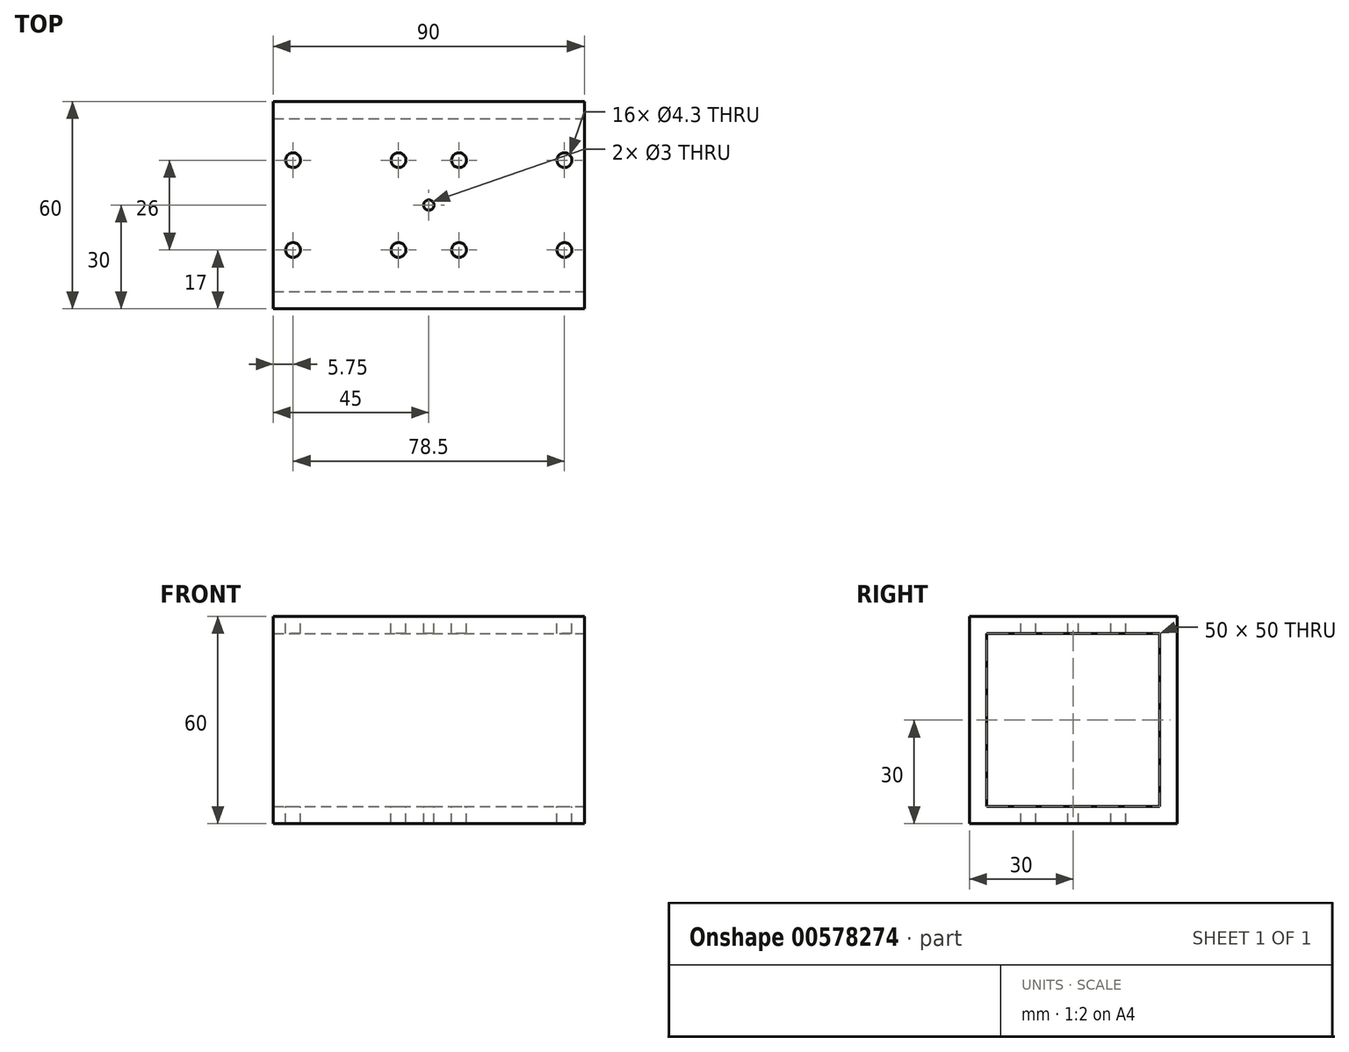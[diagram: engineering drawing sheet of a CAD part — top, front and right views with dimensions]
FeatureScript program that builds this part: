
annotation { "Feature Type Name" : "Feature", "Feature Type Description" : "" }
export const myFeature = defineFeature(function(context is Context, id is Id, definition is map)
    precondition{}
    {
        {
            var Q0;
            Q0=qCreatedBy(makeId("Top.planeOp"),FACE);
            var sketch = newSketch(context, id + "F0", { "sketchPlane" : qUnion([Q0])});
            skLineSegment(sketch, "E0.bottom", {"start": v(-45, 30) * mm, "end": v(45, 30) * mm});
            skLineSegment(sketch, "E0.top", {"start": v(-45, -30) * mm, "end": v(45, -30) * mm});
            skLineSegment(sketch, "E0.left", {"start": v(-45, 30) * mm, "end": v(-45, -30) * mm});
            skLineSegment(sketch, "E0.right", {"start": v(45, 30) * mm, "end": v(45, -30) * mm});
            skPoint(sketch, "E0.middle", {"position": v(0, 0) * mm});
            skCircle(sketch, "E1", {"center": v(-39.25, 13) * mm, "radius": 2.15 * mm});
            skCircle(sketch, "E2.MirrorC", {"center": v(-8.75, 13) * mm, "radius": 2.15 * mm});
            skCircle(sketch, "E3.MirrorC", {"center": v(-39.25, -13) * mm, "radius": 2.15 * mm});
            skCircle(sketch, "E4.MirrorC", {"center": v(-8.75, -13) * mm, "radius": 2.15 * mm});
            skCircle(sketch, "E5.MirrorC", {"center": v(39.25, 13) * mm, "radius": 2.15 * mm});
            skCircle(sketch, "E6.MirrorC", {"center": v(8.75, 13) * mm, "radius": 2.15 * mm});
            skCircle(sketch, "E7.MirrorC", {"center": v(8.75, -13) * mm, "radius": 2.15 * mm});
            skCircle(sketch, "E8.MirrorC", {"center": v(39.25, -13) * mm, "radius": 2.15 * mm});
            skSolve(sketch);
        }
        {
            var Q0;
            Q0=qSketchRegion(id+"F0",true);
            extrude(context, id + "F1", {"entities" : qUnion([Q0]), "oppositeDirection" : true, "depth" : 60 * mm, "offsetDistance" : 25 * mm});
        }
        {
            var Q0;
            Q0=makeQuery(id+"F1.opExtrude","CAP_FACE",FACE,{"disambiguationData":[OSD([sQuery(id+"F0.wireOp",EDGE,"E0.bottom"),sQuery(id+"F0.wireOp",EDGE,"E0.top"),sQuery(id+"F0.wireOp",EDGE,"E0.left"),sQuery(id+"F0.wireOp",EDGE,"E0.right"),sQuery(id+"F0.wireOp",EDGE,"E1"),sQuery(id+"F0.wireOp",EDGE,"E2.MirrorC"),sQuery(id+"F0.wireOp",EDGE,"E3.MirrorC"),sQuery(id+"F0.wireOp",EDGE,"E4.MirrorC")])],"isStart":true});
            var sketch = newSketch(context, id + "F2", { "sketchPlane" : qUnion([Q0])});
            skCircle(sketch, "E9", {"center": v(0, 0) * mm, "radius": 1.5 * mm});
            skSolve(sketch);
        }
        {
            var Q0;
            Q0=qSketchRegion(id+"F2",true);
            extrude(context, id + "F3", {"entities" : qUnion([Q0]), "operationType" : NewBodyOperationType.REMOVE, "oppositeDirection" : true, "depth" : 60 * mm, "offsetDistance" : 25 * mm});
        }
        {
            var Q0;
            Q0=makeQuery(id+"F1.opExtrude","SWEPT_FACE",FACE,{"disambiguationData":[OSD([sQuery(id+"F0.wireOp",EDGE,"E0.right")])]});
            var sketch = newSketch(context, id + "F4", { "sketchPlane" : qUnion([Q0])});
            skLineSegment(sketch, "E10", {"start": v(25, -5) * mm, "end": v(-25, -5) * mm});
            skLineSegment(sketch, "E11", {"start": v(-25, -5) * mm, "end": v(-25, -55) * mm});
            skLineSegment(sketch, "E12", {"start": v(-25, -55) * mm, "end": v(25, -55) * mm});
            skLineSegment(sketch, "E13", {"start": v(25, -5) * mm, "end": v(25, -55) * mm});
            skSolve(sketch);
        }
        {
            var Q0;
            {var subQ0=sQuery(id+"F4.wireOp",EDGE,"E10");Q0=makeQuery(id+"F4.imprint","IMPRINT",FACE,{"disambiguationData":[TD([[makeQuery(id+"F4.imprint","IMPRINT",EDGE,{"derivedFrom":subQ0}),1.0]])]});}
            extrude(context, id + "F5", {"entities" : qUnion([Q0]), "operationType" : NewBodyOperationType.REMOVE, "oppositeDirection" : true, "depth" : 90 * mm, "offsetDistance" : 25 * mm});
        }
    });
